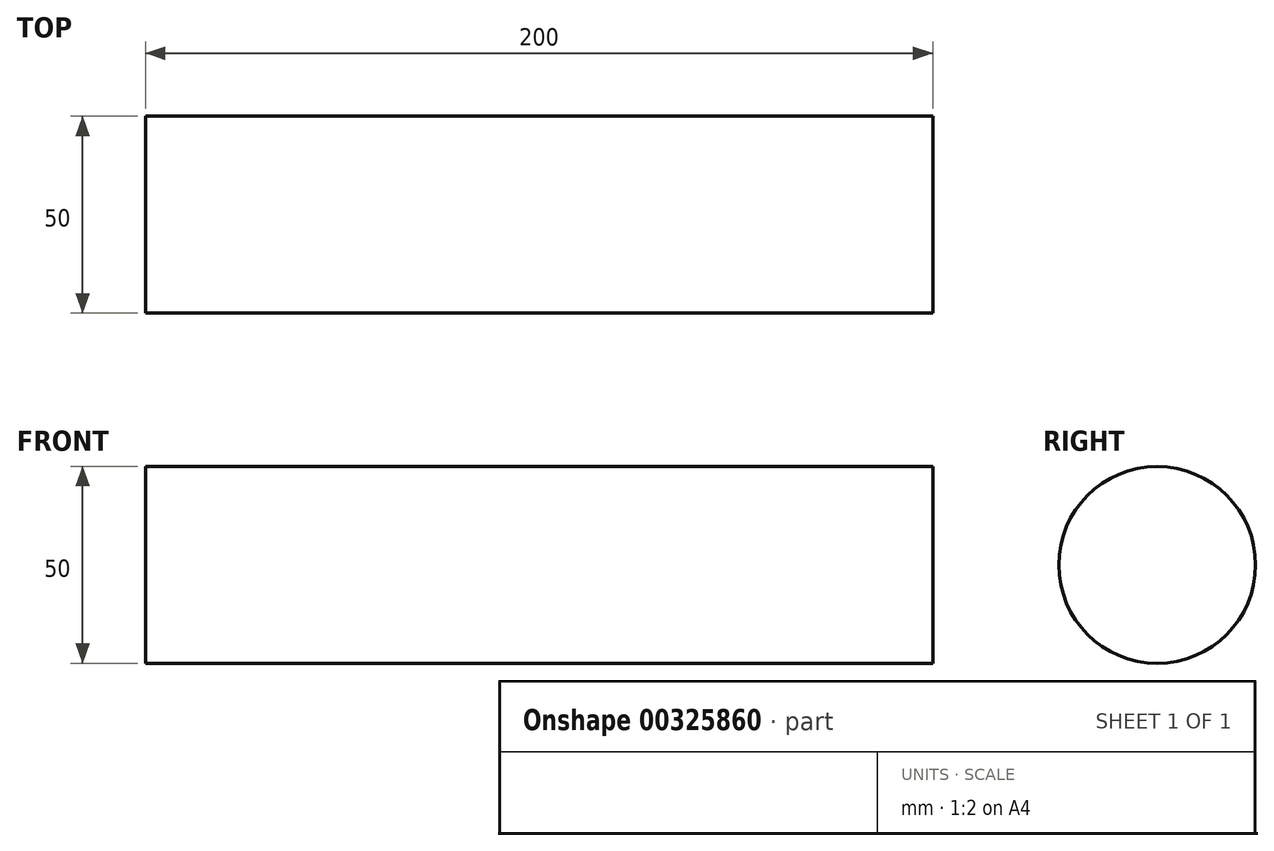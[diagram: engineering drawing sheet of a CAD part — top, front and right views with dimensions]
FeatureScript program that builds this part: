
annotation { "Feature Type Name" : "Feature", "Feature Type Description" : "" }
export const myFeature = defineFeature(function(context is Context, id is Id, definition is map)
    precondition{}
    {
        {
            var Q0;
            Q0=qCreatedBy(makeId("Right.planeOp"),FACE);
            var sketch = newSketch(context, id + "F0", { "sketchPlane" : qUnion([Q0])});
            skCircle(sketch, "E0", {"center": v(0, 0) * mm, "radius": 25 * mm});
            skSolve(sketch);
        }
        {
            var Q0;
            Q0=makeQuery(id+"F0.imprint","IMPRINT",FACE,{"disambiguationData":[TD([[makeQuery(id+"F0.imprint","IMPRINT",EDGE,{"derivedFrom":sQuery(id+"F0.wireOp",EDGE,"E0")}),1.0]])]});
            extrude(context, id + "F1", {"entities" : qUnion([Q0]), "depth" : 200 * mm});
        }
    });
